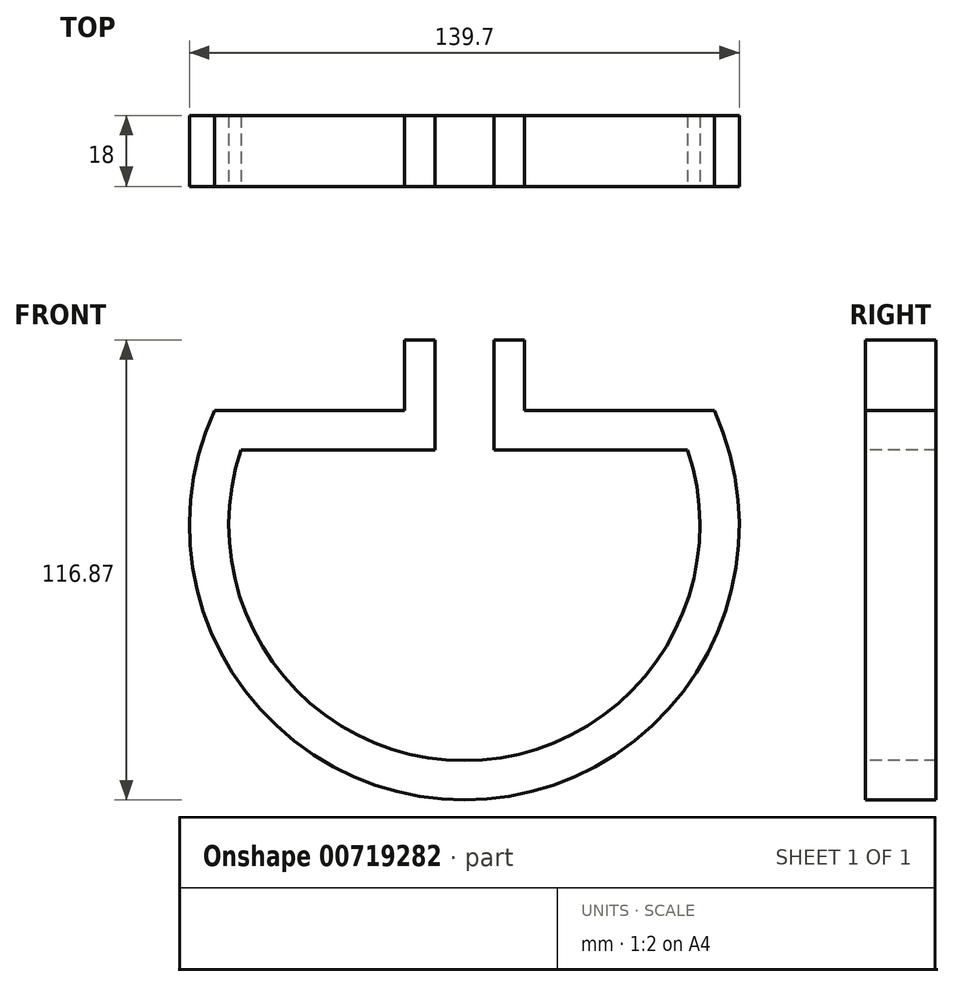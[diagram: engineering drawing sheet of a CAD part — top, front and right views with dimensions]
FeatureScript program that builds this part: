
annotation { "Feature Type Name" : "Feature", "Feature Type Description" : "" }
export const myFeature = defineFeature(function(context is Context, id is Id, definition is map)
    precondition{}
    {
        {
            var Q0;
            Q0=qCreatedBy(makeId("Front.planeOp"),FACE);
            var sketch = newSketch(context, id + "F0", { "sketchPlane" : qUnion([Q0])});
            skArc(sketch, "E0", {"start": v(-63.5, 29.1) * mm, "mid": v(0, -69.85) * mm, "end": v(63.5, 29.1) * mm});
            skLineSegment(sketch, "E1", {"start": v(0, 0) * mm, "end": v(0, 47.02) * mm, "construction": true});
            skLineSegment(sketch, "E2", {"start": v(-63.5, 29.1) * mm, "end": v(-15.24, 29.1) * mm});
            skLineSegment(sketch, "E3", {"start": v(63.5, 29.1) * mm, "end": v(15.24, 29.1) * mm});
            skLineSegment(sketch, "E4", {"start": v(-15.24, 29.1) * mm, "end": v(-15.24, 47.02) * mm});
            skLineSegment(sketch, "E5", {"start": v(-15.24, 47.02) * mm, "end": v(15.24, 47.02) * mm});
            skLineSegment(sketch, "E6", {"start": v(15.24, 29.1) * mm, "end": v(15.24, 47.02) * mm});
            skSolve(sketch);
        }
        {
            var Q0;
            Q0=makeQuery(id+"F0.imprint","IMPRINT",FACE,{"disambiguationData":[TD([[makeQuery(id+"F0.imprint","IMPRINT",EDGE,{"derivedFrom":sQuery(id+"F0.wireOp",EDGE,"E0")}),1.0]])]});
            extrude(context, id + "F1", {"entities" : qUnion([Q0]), "depth" : 18 * mm, "offsetDistance" : 25.4 * mm});
        }
        {
            var Q0;
            Q0=makeQuery(id+"F1.opExtrude","CAP_FACE",FACE,{"disambiguationData":[OSD([sQuery(id+"F0.wireOp",EDGE,"E0"),sQuery(id+"F0.wireOp",EDGE,"E2"),sQuery(id+"F0.wireOp",EDGE,"E3"),sQuery(id+"F0.wireOp",EDGE,"E4"),sQuery(id+"F0.wireOp",EDGE,"E5"),sQuery(id+"F0.wireOp",EDGE,"E6")])],"isStart":false});
            var sketch = newSketch(context, id + "F2", { "sketchPlane" : qUnion([Q0])});
            skArc(sketch, "E7.0", {"start": v(-56.72, 19.1) * mm, "mid": v(0, -59.85) * mm, "end": v(56.72, 19.1) * mm});
            skLineSegment(sketch, "E8", {"start": v(0, 0) * mm, "end": v(0, 47.02) * mm, "construction": true});
            skLineSegment(sketch, "E9", {"start": v(-7.5, 19.1) * mm, "end": v(-7.5, 47.02) * mm});
            skLineSegment(sketch, "E10", {"start": v(7.5, 19.1) * mm, "end": v(7.5, 47.02) * mm});
            skLineSegment(sketch, "E11.trimOffspring", {"start": v(7.5, 19.1) * mm, "end": v(56.72, 19.1) * mm});
            skLineSegment(sketch, "E12", {"start": v(-56.72, 19.1) * mm, "end": v(-7.5, 19.1) * mm});
            skLineSegment(sketch, "E13", {"start": v(-7.5, 47.02) * mm, "end": v(7.5, 47.02) * mm});
            skSolve(sketch);
        }
        {
            var Q0;
            Q0=makeQuery(id+"F2.imprint","IMPRINT",FACE,{"disambiguationData":[TD([[makeQuery(id+"F2.imprint","IMPRINT",EDGE,{"derivedFrom":sQuery(id+"F2.wireOp",EDGE,"E7.0")}),1.0]])]});
            extrude(context, id + "F3", {"entities" : qUnion([Q0]), "operationType" : NewBodyOperationType.REMOVE, "endBound" : BoundingType.THROUGH_ALL, "oppositeDirection" : true, "depth" : 25.4 * mm, "offsetDistance" : 25.4 * mm});
        }
    });
